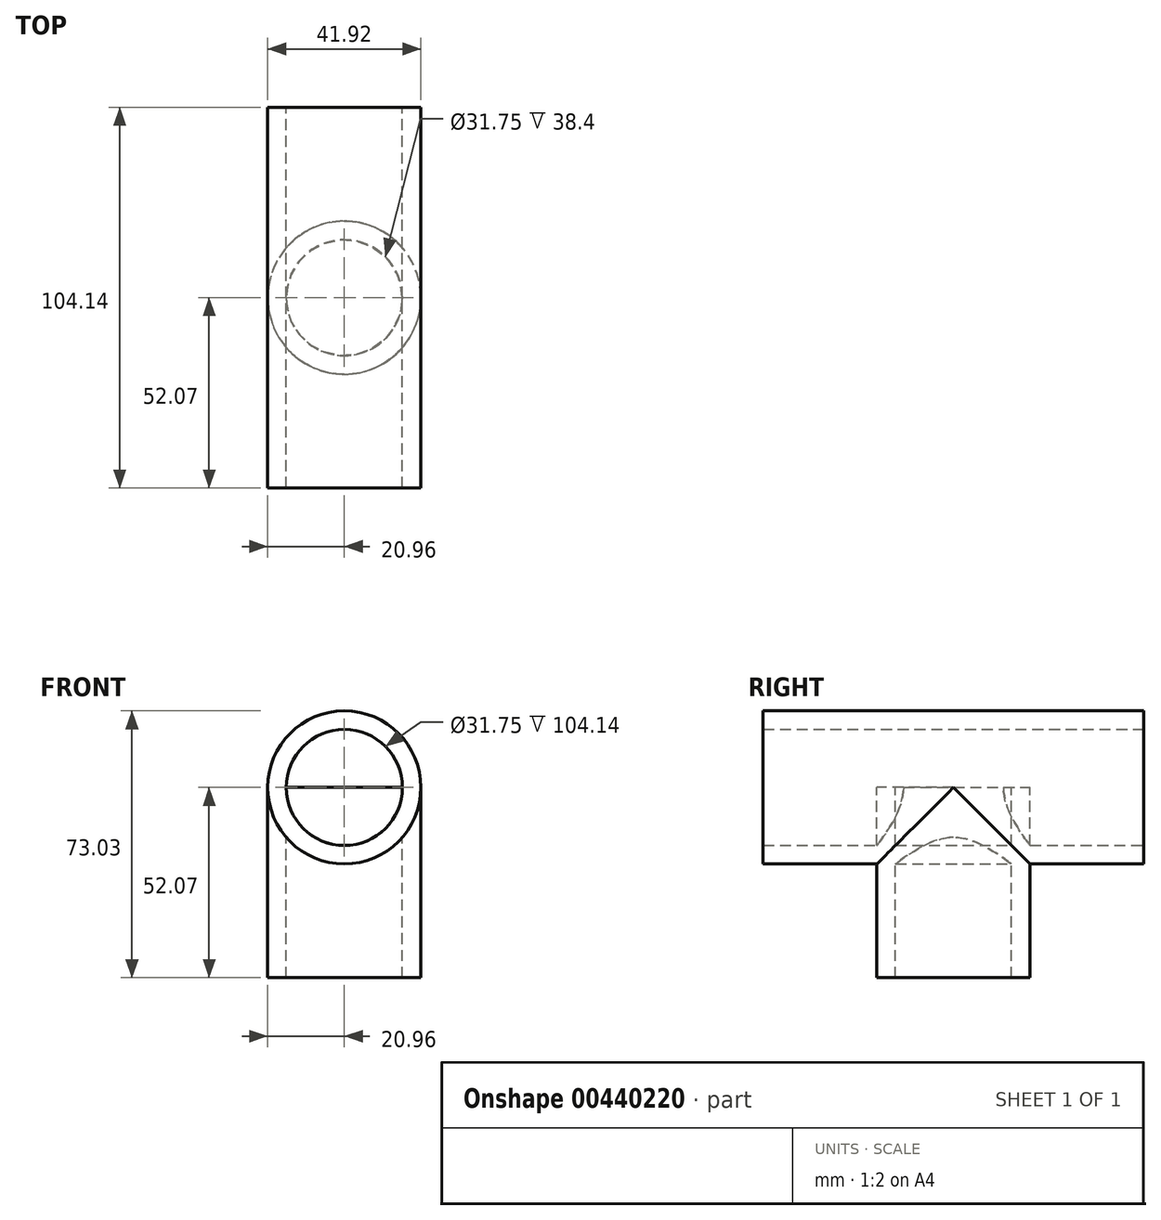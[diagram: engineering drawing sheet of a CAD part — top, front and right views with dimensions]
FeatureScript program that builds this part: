
annotation { "Feature Type Name" : "Feature", "Feature Type Description" : "" }
export const myFeature = defineFeature(function(context is Context, id is Id, definition is map)
    precondition{}
    {
        {
            var Q0;
            Q0=qCreatedBy(makeId("Top.planeOp"),FACE);
            var sketch = newSketch(context, id + "F0", { "sketchPlane" : qUnion([Q0])});
            skCircle(sketch, "E0", {"center": v(0, 0) * mm, "radius": 20.96 * mm});
            skCircle(sketch, "E1", {"center": v(0, 0) * mm, "radius": 15.88 * mm});
            skSolve(sketch);
        }
        {
            var Q0;
            Q0=makeQuery(id+"F0.imprint","IMPRINT",FACE,{"disambiguationData":[TD([[makeQuery(id+"F0.imprint","IMPRINT",EDGE,{"derivedFrom":sQuery(id+"F0.wireOp",EDGE,"E0")}),1.0]])]});
            extrude(context, id + "F1", {"entities" : qUnion([Q0]), "oppositeDirection" : true, "depth" : 52.07 * mm});
        }
        {
            var Q0;
            Q0=qCreatedBy(makeId("Front.planeOp"),FACE);
            var sketch = newSketch(context, id + "F2", { "sketchPlane" : qUnion([Q0])});
            skCircle(sketch, "E2", {"center": v(0, 0) * mm, "radius": 20.96 * mm});
            skCircle(sketch, "E3", {"center": v(0, 0) * mm, "radius": 15.88 * mm});
            skSolve(sketch);
        }
        {
            var Q0;
            Q0=makeQuery(id+"F2.imprint","IMPRINT",FACE,{"disambiguationData":[TD([[makeQuery(id+"F2.imprint","IMPRINT",EDGE,{"derivedFrom":sQuery(id+"F2.wireOp",EDGE,"E2")}),1.0]])]});
            extrude(context, id + "F3", {"entities" : qUnion([Q0]), "operationType" : NewBodyOperationType.ADD, "depth" : 52.07 * mm, "hasSecondDirection" : true, "secondDirectionOppositeDirection" : true, "secondDirectionDepth" : 52.07 * mm});
        }
    });
